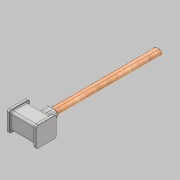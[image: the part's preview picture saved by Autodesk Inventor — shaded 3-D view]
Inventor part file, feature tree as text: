
AUTODESK INVENTOR PART (.ipt)
format: ipt  version: 2018 (Build 220112000, 112)  size: 300,544 bytes
history: native  units: mm
features: fillet x7, extrude x5, sketch x5, other x3, chamfer x3, projected_geometry x1
ambient origin geometry x8: Origin, YZ Plane, XZ Plane, XY Plane, X Axis, Y Axis, Z Axis, Center Point
bodies: Body1 (feature_tree)
feature tree (24):
  other  "實體1"
  extrude  "擠出1"  Depth=100.0mm TaperAngle=0.0deg
  fillet  "圓角1"  Radius=10.0mm
  chamfer  "倒角1"  Distance=1.0mm Angle=45.0deg
  extrude  "擠出2"  Depth=60.0mm
  extrude  "擠出3"  Depth=60.0mm
  chamfer  "倒角2"  Distance=12.0mm
  other  "刪除面1"
  other  "刪除面2"
  fillet  "圓角2"  Radius=12.0mm
  fillet  "圓角3"  Radius=12.0mm
  extrude  "擠出4"  Depth=12.0mm
  fillet  "圓角4"  Radius=120.0mm
  fillet  "圓角5"  Radius=12.0mm
  fillet  "圓角6"  Radius=1.0mm
  chamfer  "倒角3"  Distance=10.0mm
  extrude  "擠出5"  Depth=4.0mm
  fillet  "圓角7"  Radius=60.0mm
  sketch  "草圖1"
  sketch  "草圖2"
  sketch  "草圖3"
  sketch  "草圖4"
  sketch  "草圖5"
  projected_geometry  "投影迴路1"
